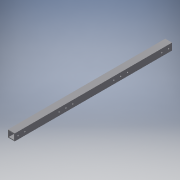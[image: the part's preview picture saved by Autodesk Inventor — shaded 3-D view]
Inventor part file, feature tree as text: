
AUTODESK INVENTOR PART (.ipt)
format: ipt  version: 2018 (Build 220112000, 112)  size: 140,288 bytes
history: native  units: in
note: dims shown in document units (in); Inventor stores cm internally (conversion verified against a paired STEP export)
features: extrude x3, sketch x3
ambient origin geometry x8: Origin, YZ Plane, XZ Plane, XY Plane, X Axis, Y Axis, Z Axis, Center Point
bodies: Solid1 (feature_tree)
feature tree (6):
  extrude  "Extrusion1"  Depth=1.0in
  extrude  "Extrusion2"  Depth=23.0in TaperAngle=0.0deg
  extrude  "Extrusion3"  Depth=1.0in
  sketch  "Sketch1"  dims[d0=1.0in d1=1.0in]
  sketch  "Sketch2"  dims[d2=0.125in d3=23.0in d4=0.0in]
  sketch  "Sketch3"  dims[d5=0.5in d6=1.0in d7=0.5in d8=1.0in d9=0.2031in d10=23.0in d11=0.0in d12=7.5in d13=0.2031in d14=1.0in d15=2.0in d16=23.0in d17=0.0in]
